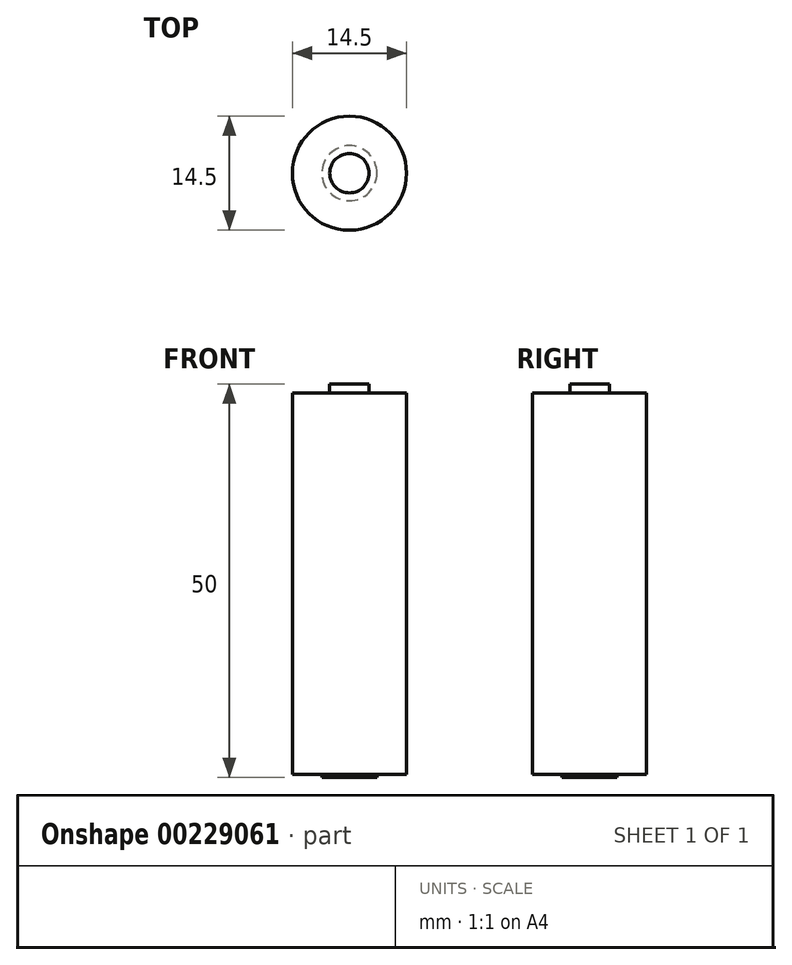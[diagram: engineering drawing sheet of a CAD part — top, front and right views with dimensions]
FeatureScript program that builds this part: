
annotation { "Feature Type Name" : "Feature", "Feature Type Description" : "" }
export const myFeature = defineFeature(function(context is Context, id is Id, definition is map)
    precondition{}
    {
        {
            var Q0;
            Q0=qCreatedBy(makeId("Top.planeOp"),FACE);
            var sketch = newSketch(context, id + "F0", { "sketchPlane" : qUnion([Q0])});
            skCircle(sketch, "E0", {"center": v(0, 0) * mm, "radius": 7.25 * mm});
            skSolve(sketch);
        }
        {
            var Q0;
            Q0 = qSketchRegion(id + "F0", true);
            extrude(context, id + "F1", {"entities" : qUnion([Q0]), "depth" : 48.4 * mm});
        }
        {
            var Q0;
            Q0=makeQuery(id+"F1.opExtrude","CAP_FACE",FACE,{"disambiguationData":[OSD([sQuery(id+"F0.wireOp",EDGE,"E0")])],"isStart":false});
            var sketch = newSketch(context, id + "F2", { "sketchPlane" : qUnion([Q0])});
            skCircle(sketch, "E1", {"center": v(0, 0) * mm, "radius": 2.5 * mm});
            skSolve(sketch);
        }
        {
            var Q0;
            Q0 = qSketchRegion(id + "F2", true);
            extrude(context, id + "F3", {"entities" : qUnion([Q0]), "operationType" : NewBodyOperationType.ADD, "depth" : 1.2 * mm});
        }
        {
            var Q0;
            Q0=makeQuery(id+"F1.opExtrude","CAP_FACE",FACE,{"disambiguationData":[OSD([sQuery(id+"F0.wireOp",EDGE,"E0")])],"isStart":true});
            var sketch = newSketch(context, id + "F4", { "sketchPlane" : qUnion([Q0])});
            skCircle(sketch, "E2", {"center": v(0, 0) * mm, "radius": 3.5 * mm});
            skSolve(sketch);
        }
        {
            var Q0;
            Q0 = qSketchRegion(id + "F4", true);
            extrude(context, id + "F5", {"entities" : qUnion([Q0]), "operationType" : NewBodyOperationType.ADD, "depth" : .4 * mm});
        }
    });
